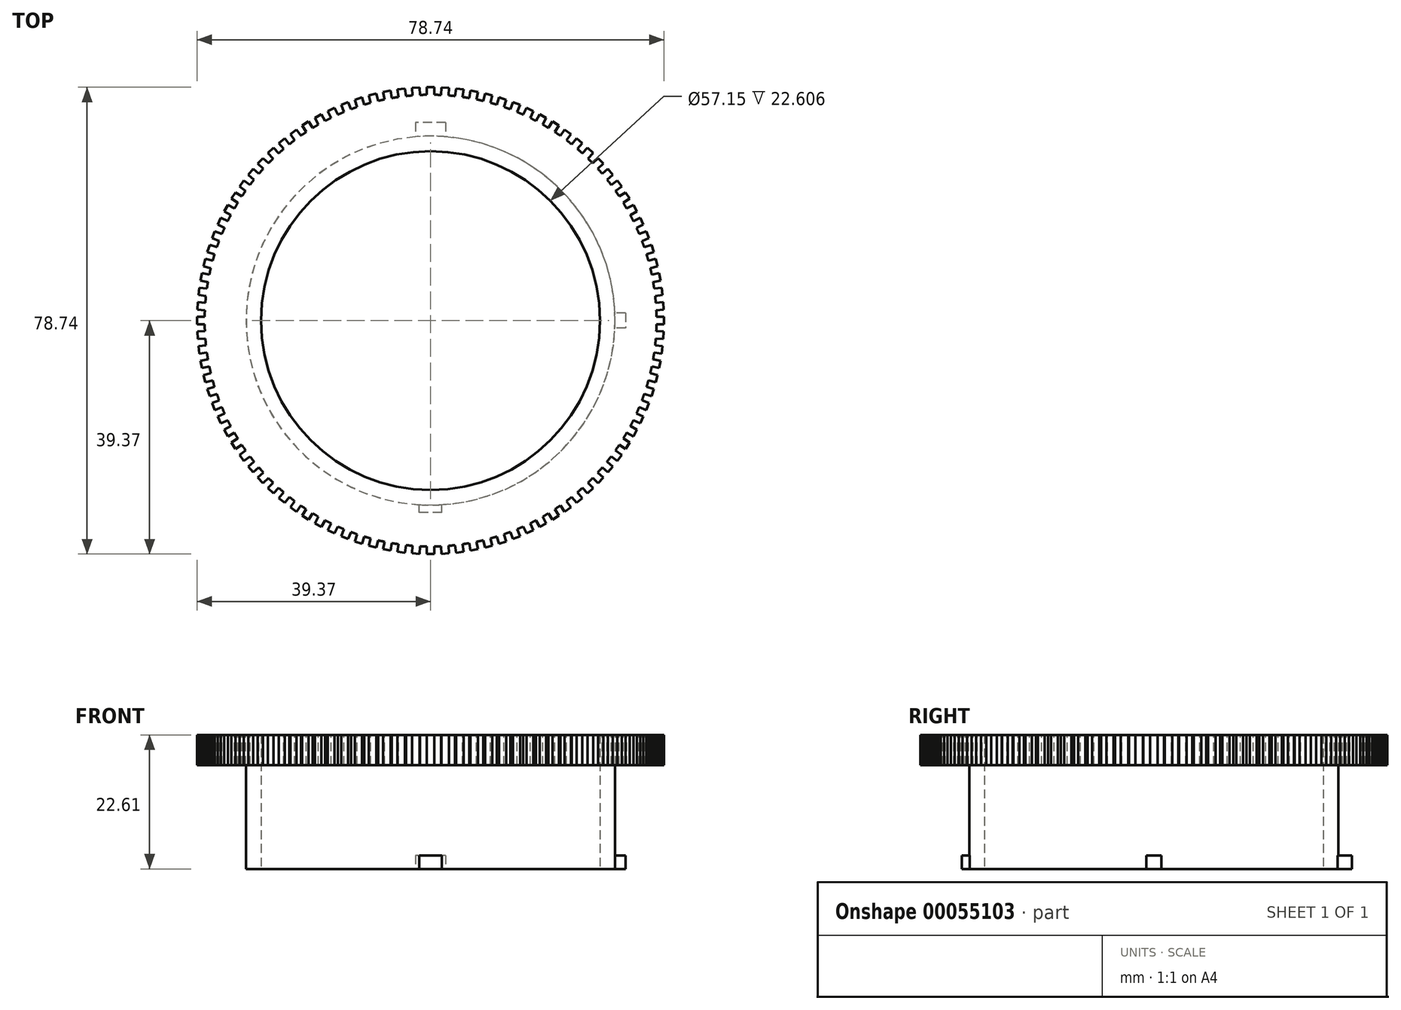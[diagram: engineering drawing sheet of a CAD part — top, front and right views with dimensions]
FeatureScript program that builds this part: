
annotation { "Feature Type Name" : "Feature", "Feature Type Description" : "" }
export const myFeature = defineFeature(function(context is Context, id is Id, definition is map)
    precondition{}
    {
        {
            var Q0;
            Q0=qCreatedBy(makeId("Top.planeOp"),FACE);
            var sketch = newSketch(context, id + "F0", { "sketchPlane" : qUnion([Q0])});
            skArc(sketch, "E0", {"start": v(-2.54, 31.01) * mm, "mid": v(-31.11, -0.32) * mm, "end": v(-1.9, -31.06) * mm});
            skLineSegment(sketch, "E1.rect.bottom", {"start": v(2.54, 33.4) * mm, "end": v(-2.54, 33.4) * mm});
            skLineSegment(sketch, "E1.rect.left", {"start": v(2.54, 33.4) * mm, "end": v(2.54, 31.01) * mm});
            skLineSegment(sketch, "E1.rect.right", {"start": v(-2.54, 33.4) * mm, "end": v(-2.54, 31.01) * mm});
            skPoint(sketch, "E1.rect.middle", {"position": v(0, 31.12) * mm});
            skLineSegment(sketch, "E2.rect.bottom", {"start": v(32.9, 1.27) * mm, "end": v(31.09, 1.27) * mm});
            skLineSegment(sketch, "E2.rect.top", {"start": v(32.9, -1.27) * mm, "end": v(31.09, -1.27) * mm});
            skLineSegment(sketch, "E2.rect.left", {"start": v(32.9, 1.27) * mm, "end": v(32.9, -1.27) * mm});
            skPoint(sketch, "E2.rect.middle", {"position": v(31.12, 0) * mm});
            skLineSegment(sketch, "E3.rect.bottom", {"start": v(1.9, -32.39) * mm, "end": v(-1.9, -32.39) * mm});
            skLineSegment(sketch, "E3.rect.left", {"start": v(1.9, -32.38) * mm, "end": v(1.9, -31.06) * mm});
            skLineSegment(sketch, "E3.rect.right", {"start": v(-1.9, -32.39) * mm, "end": v(-1.9, -31.06) * mm});
            skPoint(sketch, "E3.rect.middle", {"position": v(0, -31.12) * mm});
            skCircle(sketch, "E4", {"center": v(0, 0) * mm, "radius": 28.58 * mm});
            skPoint(sketch, "E1.rect.top.end.orphan", {"position": v(-2.54, 28.83) * mm});
            skPoint(sketch, "E5.orphan", {"position": v(2.54, 28.83) * mm});
            skArc(sketch, "E6.trimOffspring", {"start": v(31.09, 1.27) * mm, "mid": v(22.45, 21.55) * mm, "end": v(2.54, 31.01) * mm});
            skPoint(sketch, "E2.rect.right.end.orphan", {"position": v(29.34, -1.27) * mm});
            skPoint(sketch, "E2.rect.right.start.orphan", {"position": v(29.34, 1.27) * mm});
            skPoint(sketch, "E7.orphan", {"position": v(-1.9, -29.85) * mm});
            skArc(sketch, "E8.trimOffspring", {"start": v(1.9, -31.06) * mm, "mid": v(22.23, -21.78) * mm, "end": v(31.09, -1.27) * mm});
            skPoint(sketch, "E9.orphan", {"position": v(1.9, -29.85) * mm});
            skSolve(sketch);
        }
        {
            var Q0;
            Q0 = qSketchRegion(id + "F0", true);
            extrude(context, id + "F1", {"entities" : qUnion([Q0]), "depth" : 2.3 * mm});
        }
        {
            var Q0;
            Q0=makeQuery(id+"F1.opExtrude","CAP_FACE",FACE,{"disambiguationData":[OSD([sQuery(id+"F0.wireOp",EDGE,"E0"),sQuery(id+"F0.wireOp",EDGE,"E1.rect.bottom"),sQuery(id+"F0.wireOp",EDGE,"E1.rect.left"),sQuery(id+"F0.wireOp",EDGE,"E1.rect.right"),sQuery(id+"F0.wireOp",EDGE,"E2.rect.bottom"),sQuery(id+"F0.wireOp",EDGE,"E2.rect.top"),sQuery(id+"F0.wireOp",EDGE,"E2.rect.left"),sQuery(id+"F0.wireOp",EDGE,"E3.rect.bottom"),sQuery(id+"F0.wireOp",EDGE,"E3.rect.left"),sQuery(id+"F0.wireOp",EDGE,"E3.rect.right"),sQuery(id+"F0.wireOp",EDGE,"E4"),sQuery(id+"F0.wireOp",EDGE,"E6.trimOffspring"),sQuery(id+"F0.wireOp",EDGE,"E8.trimOffspring")])],"isStart":false});
            var sketch = newSketch(context, id + "F2", { "sketchPlane" : qUnion([Q0])});
            skCircle(sketch, "E10", {"center": v(0, 0) * mm, "radius": 28.58 * mm});
            skCircle(sketch, "E11", {"center": v(0, 0) * mm, "radius": 31.12 * mm});
            skSolve(sketch);
        }
        {
            var Q0;
            Q0 = qSketchRegion(id + "F2", true);
            extrude(context, id + "F3", {"entities" : qUnion([Q0]), "operationType" : NewBodyOperationType.ADD, "depth" : 16.5 * mm});
        }
        {
            var Q0;
            Q0=makeQuery(id+"F3.opExtrude","CAP_FACE",FACE,{"disambiguationData":[OSD([sQuery(id+"F2.wireOp",EDGE,"E10"),sQuery(id+"F2.wireOp",EDGE,"E11")])],"isStart":false});
            var sketch = newSketch(context, id + "F4", { "sketchPlane" : qUnion([Q0])});
            skCircle(sketch, "E12", {"center": v(0, 0) * mm, "radius": 28.57 * mm});
            skCircle(sketch, "E13", {"center": v(0, 0) * mm, "radius": 38.1 * mm});
            skSolve(sketch);
        }
        {
            var Q0;
            Q0 = qSketchRegion(id + "F4", true);
            extrude(context, id + "F5", {"entities" : qUnion([Q0]), "operationType" : NewBodyOperationType.ADD, "depth" : 3.8 * mm});
        }
        {
            var Q0;
            Q0=makeQuery(id+"F5.opExtrude","CAP_FACE",FACE,{"disambiguationData":[OSD([sQuery(id+"F4.wireOp",EDGE,"E12"),sQuery(id+"F4.wireOp",EDGE,"E13")])],"isStart":false});
            var sketch = newSketch(context, id + "F6", { "sketchPlane" : qUnion([Q0])});
            skCircle(sketch, "E14.0.0", {"center": v(0, 0) * mm, "radius": 38.1 * mm});
            skLineSegment(sketch, "E15.rect.bottom", {"start": v(0.64, -39.37) * mm, "end": v(-0.63, -39.37) * mm});
            skLineSegment(sketch, "E15.rect.left", {"start": v(0.64, -39.37) * mm, "end": v(0.64, -38.1) * mm});
            skLineSegment(sketch, "E15.rect.right", {"start": v(-0.63, -39.37) * mm, "end": v(-0.63, -38.1) * mm});
            skPoint(sketch, "E15.rect.middle", {"position": v(0, -38.1) * mm});
            skPoint(sketch, "E15.rect.top.end.orphan", {"position": v(-0.63, -36.83) * mm});
            skPoint(sketch, "E16.orphan", {"position": v(0.64, -36.83) * mm});
            skLineSegment(sketch, "E17.1.0", {"start": v(1.84, -39.33) * mm, "end": v(1.76, -38.06) * mm});
            skLineSegment(sketch, "E17.1.1", {"start": v(3.1, -39.25) * mm, "end": v(1.84, -39.33) * mm});
            skLineSegment(sketch, "E17.1.2", {"start": v(3.1, -39.25) * mm, "end": v(3.03, -37.98) * mm});
            skLineSegment(sketch, "E17.2.0", {"start": v(4.3, -39.14) * mm, "end": v(4.14, -37.87) * mm});
            skLineSegment(sketch, "E17.2.1", {"start": v(5.56, -38.98) * mm, "end": v(4.3, -39.14) * mm});
            skLineSegment(sketch, "E17.2.2", {"start": v(5.56, -38.98) * mm, "end": v(5.4, -37.71) * mm});
            skLineSegment(sketch, "E17.3.0", {"start": v(6.75, -38.8) * mm, "end": v(6.51, -37.54) * mm});
            skLineSegment(sketch, "E17.3.1", {"start": v(8, -38.55) * mm, "end": v(6.75, -38.8) * mm});
            skLineSegment(sketch, "E17.3.2", {"start": v(8, -38.55) * mm, "end": v(7.76, -37.3) * mm});
            skLineSegment(sketch, "E17.4.0", {"start": v(9.18, -38.3) * mm, "end": v(8.86, -37.06) * mm});
            skLineSegment(sketch, "E17.4.1", {"start": v(10.4, -37.98) * mm, "end": v(9.18, -38.3) * mm});
            skLineSegment(sketch, "E17.4.2", {"start": v(10.4, -37.98) * mm, "end": v(10.09, -36.74) * mm});
            skLineSegment(sketch, "E17.5.0", {"start": v(11.56, -37.64) * mm, "end": v(11.17, -36.43) * mm});
            skLineSegment(sketch, "E17.5.1", {"start": v(12.77, -37.25) * mm, "end": v(11.56, -37.64) * mm});
            skLineSegment(sketch, "E17.5.2", {"start": v(12.77, -37.25) * mm, "end": v(12.38, -36.03) * mm});
            skLineSegment(sketch, "E17.6.0", {"start": v(13.9, -36.84) * mm, "end": v(13.43, -35.65) * mm});
            skLineSegment(sketch, "E17.6.1", {"start": v(15.08, -36.37) * mm, "end": v(13.9, -36.84) * mm});
            skLineSegment(sketch, "E17.6.2", {"start": v(15.08, -36.37) * mm, "end": v(14.61, -35.19) * mm});
            skLineSegment(sketch, "E17.7.0", {"start": v(16.19, -35.9) * mm, "end": v(15.65, -34.74) * mm});
            skLineSegment(sketch, "E17.7.1", {"start": v(17.34, -35.35) * mm, "end": v(16.19, -35.9) * mm});
            skLineSegment(sketch, "E17.7.2", {"start": v(17.34, -35.35) * mm, "end": v(16.8, -34.2) * mm});
            skLineSegment(sketch, "E17.8.0", {"start": v(18.41, -34.8) * mm, "end": v(17.8, -33.69) * mm});
            skLineSegment(sketch, "E17.8.1", {"start": v(19.52, -34.2) * mm, "end": v(18.41, -34.8) * mm});
            skLineSegment(sketch, "E17.8.2", {"start": v(19.52, -34.2) * mm, "end": v(18.9, -33.08) * mm});
            skLineSegment(sketch, "E17.9.0", {"start": v(20.56, -33.58) * mm, "end": v(19.88, -32.5) * mm});
            skLineSegment(sketch, "E17.9.1", {"start": v(21.63, -32.9) * mm, "end": v(20.56, -33.58) * mm});
            skLineSegment(sketch, "E17.9.2", {"start": v(21.63, -32.9) * mm, "end": v(20.95, -31.82) * mm});
            skLineSegment(sketch, "E17.10.0", {"start": v(22.63, -32.22) * mm, "end": v(21.88, -31.2) * mm});
            skLineSegment(sketch, "E17.10.1", {"start": v(23.65, -31.48) * mm, "end": v(22.63, -32.22) * mm});
            skLineSegment(sketch, "E17.10.2", {"start": v(23.65, -31.48) * mm, "end": v(22.9, -30.45) * mm});
            skLineSegment(sketch, "E17.11.0", {"start": v(24.6, -30.74) * mm, "end": v(23.8, -29.76) * mm});
            skLineSegment(sketch, "E17.11.1", {"start": v(25.58, -29.93) * mm, "end": v(24.6, -30.74) * mm});
            skLineSegment(sketch, "E17.11.2", {"start": v(25.58, -29.93) * mm, "end": v(24.77, -28.95) * mm});
            skLineSegment(sketch, "E17.12.0", {"start": v(26.49, -29.13) * mm, "end": v(25.61, -28.2) * mm});
            skLineSegment(sketch, "E17.12.1", {"start": v(27.41, -28.26) * mm, "end": v(26.49, -29.13) * mm});
            skLineSegment(sketch, "E17.12.2", {"start": v(27.41, -28.26) * mm, "end": v(26.54, -27.34) * mm});
            skLineSegment(sketch, "E17.13.0", {"start": v(28.26, -27.41) * mm, "end": v(27.34, -26.54) * mm});
            skLineSegment(sketch, "E17.13.1", {"start": v(29.13, -26.49) * mm, "end": v(28.26, -27.41) * mm});
            skLineSegment(sketch, "E17.13.2", {"start": v(29.13, -26.49) * mm, "end": v(28.2, -25.61) * mm});
            skLineSegment(sketch, "E17.14.0", {"start": v(29.93, -25.58) * mm, "end": v(28.95, -24.77) * mm});
            skLineSegment(sketch, "E17.14.1", {"start": v(30.74, -24.6) * mm, "end": v(29.93, -25.58) * mm});
            skLineSegment(sketch, "E17.14.2", {"start": v(30.74, -24.6) * mm, "end": v(29.76, -23.8) * mm});
            skLineSegment(sketch, "E17.15.0", {"start": v(31.48, -23.65) * mm, "end": v(30.45, -22.9) * mm});
            skLineSegment(sketch, "E17.15.1", {"start": v(32.22, -22.63) * mm, "end": v(31.48, -23.65) * mm});
            skLineSegment(sketch, "E17.15.2", {"start": v(32.22, -22.63) * mm, "end": v(31.2, -21.88) * mm});
            skLineSegment(sketch, "E17.16.0", {"start": v(32.9, -21.63) * mm, "end": v(31.82, -20.95) * mm});
            skLineSegment(sketch, "E17.16.1", {"start": v(33.58, -20.56) * mm, "end": v(32.9, -21.63) * mm});
            skLineSegment(sketch, "E17.16.2", {"start": v(33.58, -20.56) * mm, "end": v(32.5, -19.88) * mm});
            skLineSegment(sketch, "E17.17.0", {"start": v(34.2, -19.52) * mm, "end": v(33.08, -18.9) * mm});
            skLineSegment(sketch, "E17.17.1", {"start": v(34.8, -18.41) * mm, "end": v(34.2, -19.52) * mm});
            skLineSegment(sketch, "E17.17.2", {"start": v(34.8, -18.41) * mm, "end": v(33.69, -17.8) * mm});
            skLineSegment(sketch, "E17.18.0", {"start": v(35.35, -17.34) * mm, "end": v(34.2, -16.8) * mm});
            skLineSegment(sketch, "E17.18.1", {"start": v(35.9, -16.19) * mm, "end": v(35.35, -17.34) * mm});
            skLineSegment(sketch, "E17.18.2", {"start": v(35.9, -16.19) * mm, "end": v(34.74, -15.65) * mm});
            skLineSegment(sketch, "E17.19.0", {"start": v(36.37, -15.08) * mm, "end": v(35.19, -14.61) * mm});
            skLineSegment(sketch, "E17.19.1", {"start": v(36.84, -13.9) * mm, "end": v(36.37, -15.08) * mm});
            skLineSegment(sketch, "E17.19.2", {"start": v(36.84, -13.9) * mm, "end": v(35.65, -13.43) * mm});
            skLineSegment(sketch, "E17.20.0", {"start": v(37.25, -12.77) * mm, "end": v(36.03, -12.38) * mm});
            skLineSegment(sketch, "E17.20.1", {"start": v(37.64, -11.56) * mm, "end": v(37.25, -12.77) * mm});
            skLineSegment(sketch, "E17.20.2", {"start": v(37.64, -11.56) * mm, "end": v(36.43, -11.17) * mm});
            skLineSegment(sketch, "E17.21.0", {"start": v(37.98, -10.4) * mm, "end": v(36.74, -10.09) * mm});
            skLineSegment(sketch, "E17.21.1", {"start": v(38.3, -9.18) * mm, "end": v(37.98, -10.4) * mm});
            skLineSegment(sketch, "E17.21.2", {"start": v(38.3, -9.18) * mm, "end": v(37.06, -8.86) * mm});
            skLineSegment(sketch, "E17.22.0", {"start": v(38.55, -8) * mm, "end": v(37.3, -7.76) * mm});
            skLineSegment(sketch, "E17.22.1", {"start": v(38.8, -6.75) * mm, "end": v(38.55, -8) * mm});
            skLineSegment(sketch, "E17.22.2", {"start": v(38.8, -6.75) * mm, "end": v(37.54, -6.51) * mm});
            skLineSegment(sketch, "E17.23.0", {"start": v(38.98, -5.56) * mm, "end": v(37.71, -5.4) * mm});
            skLineSegment(sketch, "E17.23.1", {"start": v(39.14, -4.3) * mm, "end": v(38.98, -5.56) * mm});
            skLineSegment(sketch, "E17.23.2", {"start": v(39.14, -4.3) * mm, "end": v(37.87, -4.14) * mm});
            skLineSegment(sketch, "E17.24.0", {"start": v(39.25, -3.1) * mm, "end": v(37.98, -3.03) * mm});
            skLineSegment(sketch, "E17.24.1", {"start": v(39.33, -1.84) * mm, "end": v(39.25, -3.1) * mm});
            skLineSegment(sketch, "E17.24.2", {"start": v(39.33, -1.84) * mm, "end": v(38.06, -1.76) * mm});
            skLineSegment(sketch, "E17.25.0", {"start": v(39.37, -0.63) * mm, "end": v(38.1, -0.63) * mm});
            skLineSegment(sketch, "E17.25.1", {"start": v(39.37, 0.64) * mm, "end": v(39.37, -0.63) * mm});
            skLineSegment(sketch, "E17.25.2", {"start": v(39.37, 0.64) * mm, "end": v(38.1, 0.64) * mm});
            skLineSegment(sketch, "E17.26.0", {"start": v(39.33, 1.84) * mm, "end": v(38.06, 1.76) * mm});
            skLineSegment(sketch, "E17.26.1", {"start": v(39.25, 3.1) * mm, "end": v(39.33, 1.84) * mm});
            skLineSegment(sketch, "E17.26.2", {"start": v(39.25, 3.1) * mm, "end": v(37.98, 3.03) * mm});
            skLineSegment(sketch, "E17.27.0", {"start": v(39.14, 4.3) * mm, "end": v(37.87, 4.14) * mm});
            skLineSegment(sketch, "E17.27.1", {"start": v(38.98, 5.56) * mm, "end": v(39.14, 4.3) * mm});
            skLineSegment(sketch, "E17.27.2", {"start": v(38.98, 5.56) * mm, "end": v(37.71, 5.4) * mm});
            skLineSegment(sketch, "E17.28.0", {"start": v(38.8, 6.75) * mm, "end": v(37.54, 6.51) * mm});
            skLineSegment(sketch, "E17.28.1", {"start": v(38.55, 8) * mm, "end": v(38.8, 6.75) * mm});
            skLineSegment(sketch, "E17.28.2", {"start": v(38.55, 8) * mm, "end": v(37.3, 7.76) * mm});
            skLineSegment(sketch, "E17.29.0", {"start": v(38.3, 9.18) * mm, "end": v(37.06, 8.86) * mm});
            skLineSegment(sketch, "E17.29.1", {"start": v(37.98, 10.4) * mm, "end": v(38.3, 9.18) * mm});
            skLineSegment(sketch, "E17.29.2", {"start": v(37.98, 10.4) * mm, "end": v(36.74, 10.09) * mm});
            skLineSegment(sketch, "E17.30.0", {"start": v(37.64, 11.56) * mm, "end": v(36.43, 11.17) * mm});
            skLineSegment(sketch, "E17.30.1", {"start": v(37.25, 12.77) * mm, "end": v(37.64, 11.56) * mm});
            skLineSegment(sketch, "E17.30.2", {"start": v(37.25, 12.77) * mm, "end": v(36.03, 12.38) * mm});
            skLineSegment(sketch, "E17.31.0", {"start": v(36.84, 13.9) * mm, "end": v(35.65, 13.43) * mm});
            skLineSegment(sketch, "E17.31.1", {"start": v(36.37, 15.08) * mm, "end": v(36.84, 13.9) * mm});
            skLineSegment(sketch, "E17.31.2", {"start": v(36.37, 15.08) * mm, "end": v(35.19, 14.61) * mm});
            skLineSegment(sketch, "E17.32.0", {"start": v(35.9, 16.19) * mm, "end": v(34.74, 15.65) * mm});
            skLineSegment(sketch, "E17.32.1", {"start": v(35.35, 17.34) * mm, "end": v(35.9, 16.19) * mm});
            skLineSegment(sketch, "E17.32.2", {"start": v(35.35, 17.34) * mm, "end": v(34.2, 16.8) * mm});
            skLineSegment(sketch, "E17.33.0", {"start": v(34.8, 18.41) * mm, "end": v(33.69, 17.8) * mm});
            skLineSegment(sketch, "E17.33.1", {"start": v(34.2, 19.52) * mm, "end": v(34.8, 18.41) * mm});
            skLineSegment(sketch, "E17.33.2", {"start": v(34.2, 19.52) * mm, "end": v(33.08, 18.9) * mm});
            skLineSegment(sketch, "E17.34.0", {"start": v(33.58, 20.56) * mm, "end": v(32.5, 19.88) * mm});
            skLineSegment(sketch, "E17.34.1", {"start": v(32.9, 21.63) * mm, "end": v(33.58, 20.56) * mm});
            skLineSegment(sketch, "E17.34.2", {"start": v(32.9, 21.63) * mm, "end": v(31.82, 20.95) * mm});
            skLineSegment(sketch, "E17.35.0", {"start": v(32.22, 22.63) * mm, "end": v(31.2, 21.88) * mm});
            skLineSegment(sketch, "E17.35.1", {"start": v(31.48, 23.65) * mm, "end": v(32.22, 22.63) * mm});
            skLineSegment(sketch, "E17.35.2", {"start": v(31.48, 23.65) * mm, "end": v(30.45, 22.9) * mm});
            skLineSegment(sketch, "E17.36.0", {"start": v(30.74, 24.6) * mm, "end": v(29.76, 23.8) * mm});
            skLineSegment(sketch, "E17.36.1", {"start": v(29.93, 25.58) * mm, "end": v(30.74, 24.6) * mm});
            skLineSegment(sketch, "E17.36.2", {"start": v(29.93, 25.58) * mm, "end": v(28.95, 24.77) * mm});
            skLineSegment(sketch, "E17.37.0", {"start": v(29.13, 26.49) * mm, "end": v(28.2, 25.61) * mm});
            skLineSegment(sketch, "E17.37.1", {"start": v(28.26, 27.41) * mm, "end": v(29.13, 26.49) * mm});
            skLineSegment(sketch, "E17.37.2", {"start": v(28.26, 27.41) * mm, "end": v(27.34, 26.54) * mm});
            skLineSegment(sketch, "E17.38.0", {"start": v(27.41, 28.26) * mm, "end": v(26.54, 27.34) * mm});
            skLineSegment(sketch, "E17.38.1", {"start": v(26.49, 29.13) * mm, "end": v(27.41, 28.26) * mm});
            skLineSegment(sketch, "E17.38.2", {"start": v(26.49, 29.13) * mm, "end": v(25.61, 28.2) * mm});
            skLineSegment(sketch, "E17.39.0", {"start": v(25.58, 29.93) * mm, "end": v(24.77, 28.95) * mm});
            skLineSegment(sketch, "E17.39.1", {"start": v(24.6, 30.74) * mm, "end": v(25.58, 29.93) * mm});
            skLineSegment(sketch, "E17.39.2", {"start": v(24.6, 30.74) * mm, "end": v(23.8, 29.76) * mm});
            skLineSegment(sketch, "E17.40.0", {"start": v(23.65, 31.48) * mm, "end": v(22.9, 30.45) * mm});
            skLineSegment(sketch, "E17.40.1", {"start": v(22.63, 32.22) * mm, "end": v(23.65, 31.48) * mm});
            skLineSegment(sketch, "E17.40.2", {"start": v(22.63, 32.22) * mm, "end": v(21.88, 31.2) * mm});
            skLineSegment(sketch, "E17.41.0", {"start": v(21.63, 32.9) * mm, "end": v(20.95, 31.82) * mm});
            skLineSegment(sketch, "E17.41.1", {"start": v(20.56, 33.58) * mm, "end": v(21.63, 32.9) * mm});
            skLineSegment(sketch, "E17.41.2", {"start": v(20.56, 33.58) * mm, "end": v(19.88, 32.5) * mm});
            skLineSegment(sketch, "E17.42.0", {"start": v(19.52, 34.2) * mm, "end": v(18.9, 33.08) * mm});
            skLineSegment(sketch, "E17.42.1", {"start": v(18.41, 34.8) * mm, "end": v(19.52, 34.2) * mm});
            skLineSegment(sketch, "E17.42.2", {"start": v(18.41, 34.8) * mm, "end": v(17.8, 33.69) * mm});
            skLineSegment(sketch, "E17.43.0", {"start": v(17.34, 35.35) * mm, "end": v(16.8, 34.2) * mm});
            skLineSegment(sketch, "E17.43.1", {"start": v(16.19, 35.9) * mm, "end": v(17.34, 35.35) * mm});
            skLineSegment(sketch, "E17.43.2", {"start": v(16.19, 35.9) * mm, "end": v(15.65, 34.74) * mm});
            skLineSegment(sketch, "E17.44.0", {"start": v(15.08, 36.37) * mm, "end": v(14.61, 35.19) * mm});
            skLineSegment(sketch, "E17.44.1", {"start": v(13.9, 36.84) * mm, "end": v(15.08, 36.37) * mm});
            skLineSegment(sketch, "E17.44.2", {"start": v(13.9, 36.84) * mm, "end": v(13.43, 35.65) * mm});
            skLineSegment(sketch, "E17.45.0", {"start": v(12.77, 37.25) * mm, "end": v(12.38, 36.03) * mm});
            skLineSegment(sketch, "E17.45.1", {"start": v(11.56, 37.64) * mm, "end": v(12.77, 37.25) * mm});
            skLineSegment(sketch, "E17.45.2", {"start": v(11.56, 37.64) * mm, "end": v(11.17, 36.43) * mm});
            skLineSegment(sketch, "E17.46.0", {"start": v(10.4, 37.98) * mm, "end": v(10.09, 36.74) * mm});
            skLineSegment(sketch, "E17.46.1", {"start": v(9.18, 38.3) * mm, "end": v(10.4, 37.98) * mm});
            skLineSegment(sketch, "E17.46.2", {"start": v(9.18, 38.3) * mm, "end": v(8.86, 37.06) * mm});
            skLineSegment(sketch, "E17.47.0", {"start": v(8, 38.55) * mm, "end": v(7.76, 37.3) * mm});
            skLineSegment(sketch, "E17.47.1", {"start": v(6.75, 38.8) * mm, "end": v(8, 38.55) * mm});
            skLineSegment(sketch, "E17.47.2", {"start": v(6.75, 38.8) * mm, "end": v(6.51, 37.54) * mm});
            skLineSegment(sketch, "E17.48.0", {"start": v(5.56, 38.98) * mm, "end": v(5.4, 37.71) * mm});
            skLineSegment(sketch, "E17.48.1", {"start": v(4.3, 39.14) * mm, "end": v(5.56, 38.98) * mm});
            skLineSegment(sketch, "E17.48.2", {"start": v(4.3, 39.14) * mm, "end": v(4.14, 37.87) * mm});
            skLineSegment(sketch, "E17.49.0", {"start": v(3.1, 39.25) * mm, "end": v(3.03, 37.98) * mm});
            skLineSegment(sketch, "E17.49.1", {"start": v(1.84, 39.33) * mm, "end": v(3.1, 39.25) * mm});
            skLineSegment(sketch, "E17.49.2", {"start": v(1.84, 39.33) * mm, "end": v(1.76, 38.06) * mm});
            skLineSegment(sketch, "E17.50.0", {"start": v(0.63, 39.37) * mm, "end": v(0.63, 38.1) * mm});
            skLineSegment(sketch, "E17.50.1", {"start": v(-0.64, 39.37) * mm, "end": v(0.63, 39.37) * mm});
            skLineSegment(sketch, "E17.50.2", {"start": v(-0.64, 39.37) * mm, "end": v(-0.64, 38.1) * mm});
            skLineSegment(sketch, "E17.51.0", {"start": v(-1.84, 39.33) * mm, "end": v(-1.76, 38.06) * mm});
            skLineSegment(sketch, "E17.51.1", {"start": v(-3.1, 39.25) * mm, "end": v(-1.84, 39.33) * mm});
            skLineSegment(sketch, "E17.51.2", {"start": v(-3.1, 39.25) * mm, "end": v(-3.03, 37.98) * mm});
            skLineSegment(sketch, "E17.52.0", {"start": v(-4.3, 39.14) * mm, "end": v(-4.14, 37.87) * mm});
            skLineSegment(sketch, "E17.52.1", {"start": v(-5.56, 38.98) * mm, "end": v(-4.3, 39.14) * mm});
            skLineSegment(sketch, "E17.52.2", {"start": v(-5.56, 38.98) * mm, "end": v(-5.4, 37.71) * mm});
            skLineSegment(sketch, "E17.53.0", {"start": v(-6.75, 38.8) * mm, "end": v(-6.51, 37.54) * mm});
            skLineSegment(sketch, "E17.53.1", {"start": v(-8, 38.55) * mm, "end": v(-6.75, 38.8) * mm});
            skLineSegment(sketch, "E17.53.2", {"start": v(-8, 38.55) * mm, "end": v(-7.76, 37.3) * mm});
            skLineSegment(sketch, "E17.54.0", {"start": v(-9.18, 38.3) * mm, "end": v(-8.86, 37.06) * mm});
            skLineSegment(sketch, "E17.54.1", {"start": v(-10.4, 37.98) * mm, "end": v(-9.18, 38.3) * mm});
            skLineSegment(sketch, "E17.54.2", {"start": v(-10.4, 37.98) * mm, "end": v(-10.09, 36.74) * mm});
            skLineSegment(sketch, "E17.55.0", {"start": v(-11.56, 37.64) * mm, "end": v(-11.17, 36.43) * mm});
            skLineSegment(sketch, "E17.55.1", {"start": v(-12.77, 37.25) * mm, "end": v(-11.56, 37.64) * mm});
            skLineSegment(sketch, "E17.55.2", {"start": v(-12.77, 37.25) * mm, "end": v(-12.38, 36.03) * mm});
            skLineSegment(sketch, "E17.56.0", {"start": v(-13.9, 36.84) * mm, "end": v(-13.43, 35.65) * mm});
            skLineSegment(sketch, "E17.56.1", {"start": v(-15.08, 36.37) * mm, "end": v(-13.9, 36.84) * mm});
            skLineSegment(sketch, "E17.56.2", {"start": v(-15.08, 36.37) * mm, "end": v(-14.61, 35.19) * mm});
            skLineSegment(sketch, "E17.57.0", {"start": v(-16.19, 35.9) * mm, "end": v(-15.65, 34.74) * mm});
            skLineSegment(sketch, "E17.57.1", {"start": v(-17.34, 35.35) * mm, "end": v(-16.19, 35.9) * mm});
            skLineSegment(sketch, "E17.57.2", {"start": v(-17.34, 35.35) * mm, "end": v(-16.8, 34.2) * mm});
            skLineSegment(sketch, "E17.58.0", {"start": v(-18.41, 34.8) * mm, "end": v(-17.8, 33.69) * mm});
            skLineSegment(sketch, "E17.58.1", {"start": v(-19.52, 34.2) * mm, "end": v(-18.41, 34.8) * mm});
            skLineSegment(sketch, "E17.58.2", {"start": v(-19.52, 34.2) * mm, "end": v(-18.9, 33.08) * mm});
            skLineSegment(sketch, "E17.59.0", {"start": v(-20.56, 33.58) * mm, "end": v(-19.88, 32.5) * mm});
            skLineSegment(sketch, "E17.59.1", {"start": v(-21.63, 32.9) * mm, "end": v(-20.56, 33.58) * mm});
            skLineSegment(sketch, "E17.59.2", {"start": v(-21.63, 32.9) * mm, "end": v(-20.95, 31.82) * mm});
            skLineSegment(sketch, "E17.60.0", {"start": v(-22.63, 32.22) * mm, "end": v(-21.88, 31.2) * mm});
            skLineSegment(sketch, "E17.60.1", {"start": v(-23.65, 31.48) * mm, "end": v(-22.63, 32.22) * mm});
            skLineSegment(sketch, "E17.60.2", {"start": v(-23.65, 31.48) * mm, "end": v(-22.9, 30.45) * mm});
            skLineSegment(sketch, "E17.61.0", {"start": v(-24.6, 30.74) * mm, "end": v(-23.8, 29.76) * mm});
            skLineSegment(sketch, "E17.61.1", {"start": v(-25.58, 29.93) * mm, "end": v(-24.6, 30.74) * mm});
            skLineSegment(sketch, "E17.61.2", {"start": v(-25.58, 29.93) * mm, "end": v(-24.77, 28.95) * mm});
            skLineSegment(sketch, "E17.62.0", {"start": v(-26.49, 29.13) * mm, "end": v(-25.61, 28.2) * mm});
            skLineSegment(sketch, "E17.62.1", {"start": v(-27.41, 28.26) * mm, "end": v(-26.49, 29.13) * mm});
            skLineSegment(sketch, "E17.62.2", {"start": v(-27.41, 28.26) * mm, "end": v(-26.54, 27.34) * mm});
            skLineSegment(sketch, "E17.63.0", {"start": v(-28.26, 27.41) * mm, "end": v(-27.34, 26.54) * mm});
            skLineSegment(sketch, "E17.63.1", {"start": v(-29.13, 26.49) * mm, "end": v(-28.26, 27.41) * mm});
            skLineSegment(sketch, "E17.63.2", {"start": v(-29.13, 26.49) * mm, "end": v(-28.2, 25.61) * mm});
            skLineSegment(sketch, "E17.64.0", {"start": v(-29.93, 25.58) * mm, "end": v(-28.95, 24.77) * mm});
            skLineSegment(sketch, "E17.64.1", {"start": v(-30.74, 24.6) * mm, "end": v(-29.93, 25.58) * mm});
            skLineSegment(sketch, "E17.64.2", {"start": v(-30.74, 24.6) * mm, "end": v(-29.76, 23.8) * mm});
            skLineSegment(sketch, "E17.65.0", {"start": v(-31.48, 23.65) * mm, "end": v(-30.45, 22.9) * mm});
            skLineSegment(sketch, "E17.65.1", {"start": v(-32.22, 22.63) * mm, "end": v(-31.48, 23.65) * mm});
            skLineSegment(sketch, "E17.65.2", {"start": v(-32.22, 22.63) * mm, "end": v(-31.2, 21.88) * mm});
            skLineSegment(sketch, "E17.66.0", {"start": v(-32.9, 21.63) * mm, "end": v(-31.82, 20.95) * mm});
            skLineSegment(sketch, "E17.66.1", {"start": v(-33.58, 20.56) * mm, "end": v(-32.9, 21.63) * mm});
            skLineSegment(sketch, "E17.66.2", {"start": v(-33.58, 20.56) * mm, "end": v(-32.5, 19.88) * mm});
            skLineSegment(sketch, "E17.67.0", {"start": v(-34.2, 19.52) * mm, "end": v(-33.08, 18.9) * mm});
            skLineSegment(sketch, "E17.67.1", {"start": v(-34.8, 18.41) * mm, "end": v(-34.2, 19.52) * mm});
            skLineSegment(sketch, "E17.67.2", {"start": v(-34.8, 18.41) * mm, "end": v(-33.69, 17.8) * mm});
            skLineSegment(sketch, "E17.68.0", {"start": v(-35.35, 17.34) * mm, "end": v(-34.2, 16.8) * mm});
            skLineSegment(sketch, "E17.68.1", {"start": v(-35.9, 16.19) * mm, "end": v(-35.35, 17.34) * mm});
            skLineSegment(sketch, "E17.68.2", {"start": v(-35.9, 16.19) * mm, "end": v(-34.74, 15.65) * mm});
            skLineSegment(sketch, "E17.69.0", {"start": v(-36.37, 15.08) * mm, "end": v(-35.19, 14.61) * mm});
            skLineSegment(sketch, "E17.69.1", {"start": v(-36.84, 13.9) * mm, "end": v(-36.37, 15.08) * mm});
            skLineSegment(sketch, "E17.69.2", {"start": v(-36.84, 13.9) * mm, "end": v(-35.65, 13.43) * mm});
            skLineSegment(sketch, "E17.70.0", {"start": v(-37.25, 12.77) * mm, "end": v(-36.03, 12.38) * mm});
            skLineSegment(sketch, "E17.70.1", {"start": v(-37.64, 11.56) * mm, "end": v(-37.25, 12.77) * mm});
            skLineSegment(sketch, "E17.70.2", {"start": v(-37.64, 11.56) * mm, "end": v(-36.43, 11.17) * mm});
            skLineSegment(sketch, "E17.71.0", {"start": v(-37.98, 10.4) * mm, "end": v(-36.74, 10.09) * mm});
            skLineSegment(sketch, "E17.71.1", {"start": v(-38.3, 9.18) * mm, "end": v(-37.98, 10.4) * mm});
            skLineSegment(sketch, "E17.71.2", {"start": v(-38.3, 9.18) * mm, "end": v(-37.06, 8.86) * mm});
            skLineSegment(sketch, "E17.72.0", {"start": v(-38.55, 8) * mm, "end": v(-37.3, 7.76) * mm});
            skLineSegment(sketch, "E17.72.1", {"start": v(-38.8, 6.75) * mm, "end": v(-38.55, 8) * mm});
            skLineSegment(sketch, "E17.72.2", {"start": v(-38.8, 6.75) * mm, "end": v(-37.54, 6.51) * mm});
            skLineSegment(sketch, "E17.73.0", {"start": v(-38.98, 5.56) * mm, "end": v(-37.71, 5.4) * mm});
            skLineSegment(sketch, "E17.73.1", {"start": v(-39.14, 4.3) * mm, "end": v(-38.98, 5.56) * mm});
            skLineSegment(sketch, "E17.73.2", {"start": v(-39.14, 4.3) * mm, "end": v(-37.87, 4.14) * mm});
            skLineSegment(sketch, "E17.74.0", {"start": v(-39.25, 3.1) * mm, "end": v(-37.98, 3.03) * mm});
            skLineSegment(sketch, "E17.74.1", {"start": v(-39.33, 1.84) * mm, "end": v(-39.25, 3.1) * mm});
            skLineSegment(sketch, "E17.74.2", {"start": v(-39.33, 1.84) * mm, "end": v(-38.06, 1.76) * mm});
            skLineSegment(sketch, "E17.75.0", {"start": v(-39.37, 0.64) * mm, "end": v(-38.1, 0.63) * mm});
            skLineSegment(sketch, "E17.75.1", {"start": v(-39.37, -0.63) * mm, "end": v(-39.37, 0.64) * mm});
            skLineSegment(sketch, "E17.75.2", {"start": v(-39.37, -0.64) * mm, "end": v(-38.1, -0.64) * mm});
            skLineSegment(sketch, "E17.76.0", {"start": v(-39.33, -1.84) * mm, "end": v(-38.06, -1.76) * mm});
            skLineSegment(sketch, "E17.76.1", {"start": v(-39.25, -3.1) * mm, "end": v(-39.33, -1.84) * mm});
            skLineSegment(sketch, "E17.76.2", {"start": v(-39.25, -3.1) * mm, "end": v(-37.98, -3.03) * mm});
            skLineSegment(sketch, "E17.77.0", {"start": v(-39.14, -4.3) * mm, "end": v(-37.87, -4.14) * mm});
            skLineSegment(sketch, "E17.77.1", {"start": v(-38.98, -5.56) * mm, "end": v(-39.14, -4.3) * mm});
            skLineSegment(sketch, "E17.77.2", {"start": v(-38.98, -5.56) * mm, "end": v(-37.71, -5.4) * mm});
            skLineSegment(sketch, "E17.78.0", {"start": v(-38.8, -6.75) * mm, "end": v(-37.54, -6.51) * mm});
            skLineSegment(sketch, "E17.78.1", {"start": v(-38.55, -8) * mm, "end": v(-38.8, -6.75) * mm});
            skLineSegment(sketch, "E17.78.2", {"start": v(-38.55, -8) * mm, "end": v(-37.3, -7.76) * mm});
            skLineSegment(sketch, "E17.79.0", {"start": v(-38.3, -9.18) * mm, "end": v(-37.06, -8.86) * mm});
            skLineSegment(sketch, "E17.79.1", {"start": v(-37.98, -10.4) * mm, "end": v(-38.3, -9.18) * mm});
            skLineSegment(sketch, "E17.79.2", {"start": v(-37.98, -10.4) * mm, "end": v(-36.74, -10.09) * mm});
            skLineSegment(sketch, "E17.80.0", {"start": v(-37.64, -11.56) * mm, "end": v(-36.43, -11.17) * mm});
            skLineSegment(sketch, "E17.80.1", {"start": v(-37.25, -12.77) * mm, "end": v(-37.64, -11.56) * mm});
            skLineSegment(sketch, "E17.80.2", {"start": v(-37.25, -12.77) * mm, "end": v(-36.03, -12.38) * mm});
            skLineSegment(sketch, "E17.81.0", {"start": v(-36.84, -13.9) * mm, "end": v(-35.65, -13.43) * mm});
            skLineSegment(sketch, "E17.81.1", {"start": v(-36.37, -15.08) * mm, "end": v(-36.84, -13.9) * mm});
            skLineSegment(sketch, "E17.81.2", {"start": v(-36.37, -15.08) * mm, "end": v(-35.19, -14.61) * mm});
            skLineSegment(sketch, "E17.82.0", {"start": v(-35.9, -16.19) * mm, "end": v(-34.74, -15.65) * mm});
            skLineSegment(sketch, "E17.82.1", {"start": v(-35.35, -17.34) * mm, "end": v(-35.9, -16.19) * mm});
            skLineSegment(sketch, "E17.82.2", {"start": v(-35.35, -17.34) * mm, "end": v(-34.2, -16.8) * mm});
            skLineSegment(sketch, "E17.83.0", {"start": v(-34.8, -18.41) * mm, "end": v(-33.69, -17.8) * mm});
            skLineSegment(sketch, "E17.83.1", {"start": v(-34.2, -19.52) * mm, "end": v(-34.8, -18.41) * mm});
            skLineSegment(sketch, "E17.83.2", {"start": v(-34.2, -19.52) * mm, "end": v(-33.08, -18.9) * mm});
            skLineSegment(sketch, "E17.84.0", {"start": v(-33.58, -20.56) * mm, "end": v(-32.5, -19.88) * mm});
            skLineSegment(sketch, "E17.84.1", {"start": v(-32.9, -21.63) * mm, "end": v(-33.58, -20.56) * mm});
            skLineSegment(sketch, "E17.84.2", {"start": v(-32.9, -21.63) * mm, "end": v(-31.82, -20.95) * mm});
            skLineSegment(sketch, "E17.85.0", {"start": v(-32.22, -22.63) * mm, "end": v(-31.2, -21.88) * mm});
            skLineSegment(sketch, "E17.85.1", {"start": v(-31.48, -23.65) * mm, "end": v(-32.22, -22.63) * mm});
            skLineSegment(sketch, "E17.85.2", {"start": v(-31.48, -23.65) * mm, "end": v(-30.45, -22.9) * mm});
            skLineSegment(sketch, "E17.86.0", {"start": v(-30.74, -24.6) * mm, "end": v(-29.76, -23.8) * mm});
            skLineSegment(sketch, "E17.86.1", {"start": v(-29.93, -25.58) * mm, "end": v(-30.74, -24.6) * mm});
            skLineSegment(sketch, "E17.86.2", {"start": v(-29.93, -25.58) * mm, "end": v(-28.95, -24.77) * mm});
            skLineSegment(sketch, "E17.87.0", {"start": v(-29.13, -26.49) * mm, "end": v(-28.2, -25.61) * mm});
            skLineSegment(sketch, "E17.87.1", {"start": v(-28.26, -27.41) * mm, "end": v(-29.13, -26.49) * mm});
            skLineSegment(sketch, "E17.87.2", {"start": v(-28.26, -27.41) * mm, "end": v(-27.34, -26.54) * mm});
            skLineSegment(sketch, "E17.88.0", {"start": v(-27.41, -28.26) * mm, "end": v(-26.54, -27.34) * mm});
            skLineSegment(sketch, "E17.88.1", {"start": v(-26.49, -29.13) * mm, "end": v(-27.41, -28.26) * mm});
            skLineSegment(sketch, "E17.88.2", {"start": v(-26.49, -29.13) * mm, "end": v(-25.61, -28.2) * mm});
            skLineSegment(sketch, "E17.89.0", {"start": v(-25.58, -29.93) * mm, "end": v(-24.77, -28.95) * mm});
            skLineSegment(sketch, "E17.89.1", {"start": v(-24.6, -30.74) * mm, "end": v(-25.58, -29.93) * mm});
            skLineSegment(sketch, "E17.89.2", {"start": v(-24.6, -30.74) * mm, "end": v(-23.8, -29.76) * mm});
            skLineSegment(sketch, "E17.90.0", {"start": v(-23.65, -31.48) * mm, "end": v(-22.9, -30.45) * mm});
            skLineSegment(sketch, "E17.90.1", {"start": v(-22.63, -32.22) * mm, "end": v(-23.65, -31.48) * mm});
            skLineSegment(sketch, "E17.90.2", {"start": v(-22.63, -32.22) * mm, "end": v(-21.88, -31.2) * mm});
            skLineSegment(sketch, "E17.91.0", {"start": v(-21.63, -32.9) * mm, "end": v(-20.95, -31.82) * mm});
            skLineSegment(sketch, "E17.91.1", {"start": v(-20.56, -33.58) * mm, "end": v(-21.63, -32.9) * mm});
            skLineSegment(sketch, "E17.91.2", {"start": v(-20.56, -33.58) * mm, "end": v(-19.88, -32.5) * mm});
            skLineSegment(sketch, "E17.92.0", {"start": v(-19.52, -34.2) * mm, "end": v(-18.9, -33.08) * mm});
            skLineSegment(sketch, "E17.92.1", {"start": v(-18.41, -34.8) * mm, "end": v(-19.52, -34.2) * mm});
            skLineSegment(sketch, "E17.92.2", {"start": v(-18.41, -34.8) * mm, "end": v(-17.8, -33.69) * mm});
            skLineSegment(sketch, "E17.93.0", {"start": v(-17.34, -35.35) * mm, "end": v(-16.8, -34.2) * mm});
            skLineSegment(sketch, "E17.93.1", {"start": v(-16.19, -35.9) * mm, "end": v(-17.34, -35.35) * mm});
            skLineSegment(sketch, "E17.93.2", {"start": v(-16.19, -35.9) * mm, "end": v(-15.65, -34.74) * mm});
            skLineSegment(sketch, "E17.94.0", {"start": v(-15.08, -36.37) * mm, "end": v(-14.61, -35.19) * mm});
            skLineSegment(sketch, "E17.94.1", {"start": v(-13.9, -36.84) * mm, "end": v(-15.08, -36.37) * mm});
            skLineSegment(sketch, "E17.94.2", {"start": v(-13.9, -36.84) * mm, "end": v(-13.43, -35.65) * mm});
            skLineSegment(sketch, "E17.95.0", {"start": v(-12.77, -37.25) * mm, "end": v(-12.38, -36.03) * mm});
            skLineSegment(sketch, "E17.95.1", {"start": v(-11.56, -37.64) * mm, "end": v(-12.77, -37.25) * mm});
            skLineSegment(sketch, "E17.95.2", {"start": v(-11.56, -37.64) * mm, "end": v(-11.17, -36.43) * mm});
            skLineSegment(sketch, "E17.96.0", {"start": v(-10.4, -37.98) * mm, "end": v(-10.09, -36.74) * mm});
            skLineSegment(sketch, "E17.96.1", {"start": v(-9.18, -38.3) * mm, "end": v(-10.4, -37.98) * mm});
            skLineSegment(sketch, "E17.96.2", {"start": v(-9.18, -38.3) * mm, "end": v(-8.86, -37.06) * mm});
            skLineSegment(sketch, "E17.97.0", {"start": v(-8, -38.55) * mm, "end": v(-7.76, -37.3) * mm});
            skLineSegment(sketch, "E17.97.1", {"start": v(-6.75, -38.8) * mm, "end": v(-8, -38.55) * mm});
            skLineSegment(sketch, "E17.97.2", {"start": v(-6.75, -38.8) * mm, "end": v(-6.51, -37.54) * mm});
            skLineSegment(sketch, "E17.98.0", {"start": v(-5.56, -38.98) * mm, "end": v(-5.4, -37.71) * mm});
            skLineSegment(sketch, "E17.98.1", {"start": v(-4.3, -39.14) * mm, "end": v(-5.56, -38.98) * mm});
            skLineSegment(sketch, "E17.98.2", {"start": v(-4.3, -39.14) * mm, "end": v(-4.14, -37.87) * mm});
            skLineSegment(sketch, "E17.99.0", {"start": v(-3.1, -39.25) * mm, "end": v(-3.03, -37.98) * mm});
            skLineSegment(sketch, "E17.99.1", {"start": v(-1.84, -39.33) * mm, "end": v(-3.1, -39.25) * mm});
            skLineSegment(sketch, "E17.99.2", {"start": v(-1.84, -39.33) * mm, "end": v(-1.76, -38.06) * mm});
            skSolve(sketch);
        }
        {
            var Q0;
            Q0=makeQuery(id+"F6.imprint","IMPRINT",FACE,{"disambiguationData":[TD([[makeQuery(id+"F6.imprint","IMPRINT",EDGE,{"derivedFrom":sQuery(id+"F6.wireOp",EDGE,"E15.rect.bottom")}),-1.0]])]});
            var Q1;
            {var subQ0=sQuery(id+"F6.wireOp",EDGE,"E17.1.0");Q1=makeQuery(id+"F6.imprint","IMPRINT",FACE,{"disambiguationData":[TD([[makeQuery(id+"F6.imprint","IMPRINT",EDGE,{"derivedFrom":subQ0}),-1.0]])]});}
            var Q2;
            {var subQ0=sQuery(id+"F6.wireOp",EDGE,"E17.2.0");Q2=makeQuery(id+"F6.imprint","IMPRINT",FACE,{"disambiguationData":[TD([[makeQuery(id+"F6.imprint","IMPRINT",EDGE,{"derivedFrom":subQ0}),-1.0]])]});}
            var Q3;
            {var subQ0=sQuery(id+"F6.wireOp",EDGE,"E17.3.0");Q3=makeQuery(id+"F6.imprint","IMPRINT",FACE,{"disambiguationData":[TD([[makeQuery(id+"F6.imprint","IMPRINT",EDGE,{"derivedFrom":subQ0}),-1.0]])]});}
            var Q4;
            {var subQ0=sQuery(id+"F6.wireOp",EDGE,"E17.4.0");Q4=makeQuery(id+"F6.imprint","IMPRINT",FACE,{"disambiguationData":[TD([[makeQuery(id+"F6.imprint","IMPRINT",EDGE,{"derivedFrom":subQ0}),-1.0]])]});}
            var Q5;
            {var subQ0=sQuery(id+"F6.wireOp",EDGE,"E17.5.0");Q5=makeQuery(id+"F6.imprint","IMPRINT",FACE,{"disambiguationData":[TD([[makeQuery(id+"F6.imprint","IMPRINT",EDGE,{"derivedFrom":subQ0}),-1.0]])]});}
            var Q6;
            {var subQ0=sQuery(id+"F6.wireOp",EDGE,"E17.6.0");Q6=makeQuery(id+"F6.imprint","IMPRINT",FACE,{"disambiguationData":[TD([[makeQuery(id+"F6.imprint","IMPRINT",EDGE,{"derivedFrom":subQ0}),-1.0]])]});}
            var Q7;
            {var subQ0=sQuery(id+"F6.wireOp",EDGE,"E17.7.0");Q7=makeQuery(id+"F6.imprint","IMPRINT",FACE,{"disambiguationData":[TD([[makeQuery(id+"F6.imprint","IMPRINT",EDGE,{"derivedFrom":subQ0}),-1.0]])]});}
            var Q8;
            {var subQ0=sQuery(id+"F6.wireOp",EDGE,"E17.8.0");Q8=makeQuery(id+"F6.imprint","IMPRINT",FACE,{"disambiguationData":[TD([[makeQuery(id+"F6.imprint","IMPRINT",EDGE,{"derivedFrom":subQ0}),-1.0]])]});}
            var Q9;
            {var subQ0=sQuery(id+"F6.wireOp",EDGE,"E17.9.0");Q9=makeQuery(id+"F6.imprint","IMPRINT",FACE,{"disambiguationData":[TD([[makeQuery(id+"F6.imprint","IMPRINT",EDGE,{"derivedFrom":subQ0}),-1.0]])]});}
            var Q10;
            {var subQ0=sQuery(id+"F6.wireOp",EDGE,"E17.10.0");Q10=makeQuery(id+"F6.imprint","IMPRINT",FACE,{"disambiguationData":[TD([[makeQuery(id+"F6.imprint","IMPRINT",EDGE,{"derivedFrom":subQ0}),-1.0]])]});}
            var Q11;
            {var subQ0=sQuery(id+"F6.wireOp",EDGE,"E17.11.0");Q11=makeQuery(id+"F6.imprint","IMPRINT",FACE,{"disambiguationData":[TD([[makeQuery(id+"F6.imprint","IMPRINT",EDGE,{"derivedFrom":subQ0}),-1.0]])]});}
            var Q12;
            {var subQ0=sQuery(id+"F6.wireOp",EDGE,"E17.12.0");Q12=makeQuery(id+"F6.imprint","IMPRINT",FACE,{"disambiguationData":[TD([[makeQuery(id+"F6.imprint","IMPRINT",EDGE,{"derivedFrom":subQ0}),-1.0]])]});}
            var Q13;
            {var subQ0=sQuery(id+"F6.wireOp",EDGE,"E17.13.0");Q13=makeQuery(id+"F6.imprint","IMPRINT",FACE,{"disambiguationData":[TD([[makeQuery(id+"F6.imprint","IMPRINT",EDGE,{"derivedFrom":subQ0}),-1.0]])]});}
            var Q14;
            {var subQ0=sQuery(id+"F6.wireOp",EDGE,"E17.14.0");Q14=makeQuery(id+"F6.imprint","IMPRINT",FACE,{"disambiguationData":[TD([[makeQuery(id+"F6.imprint","IMPRINT",EDGE,{"derivedFrom":subQ0}),-1.0]])]});}
            var Q15;
            {var subQ0=sQuery(id+"F6.wireOp",EDGE,"E17.15.0");Q15=makeQuery(id+"F6.imprint","IMPRINT",FACE,{"disambiguationData":[TD([[makeQuery(id+"F6.imprint","IMPRINT",EDGE,{"derivedFrom":subQ0}),-1.0]])]});}
            var Q16;
            {var subQ0=sQuery(id+"F6.wireOp",EDGE,"E17.16.0");Q16=makeQuery(id+"F6.imprint","IMPRINT",FACE,{"disambiguationData":[TD([[makeQuery(id+"F6.imprint","IMPRINT",EDGE,{"derivedFrom":subQ0}),-1.0]])]});}
            var Q17;
            {var subQ0=sQuery(id+"F6.wireOp",EDGE,"E17.17.0");Q17=makeQuery(id+"F6.imprint","IMPRINT",FACE,{"disambiguationData":[TD([[makeQuery(id+"F6.imprint","IMPRINT",EDGE,{"derivedFrom":subQ0}),-1.0]])]});}
            var Q18;
            {var subQ0=sQuery(id+"F6.wireOp",EDGE,"E17.18.0");Q18=makeQuery(id+"F6.imprint","IMPRINT",FACE,{"disambiguationData":[TD([[makeQuery(id+"F6.imprint","IMPRINT",EDGE,{"derivedFrom":subQ0}),-1.0]])]});}
            var Q19;
            {var subQ0=sQuery(id+"F6.wireOp",EDGE,"E17.19.0");Q19=makeQuery(id+"F6.imprint","IMPRINT",FACE,{"disambiguationData":[TD([[makeQuery(id+"F6.imprint","IMPRINT",EDGE,{"derivedFrom":subQ0}),-1.0]])]});}
            var Q20;
            {var subQ0=sQuery(id+"F6.wireOp",EDGE,"E17.20.0");Q20=makeQuery(id+"F6.imprint","IMPRINT",FACE,{"disambiguationData":[TD([[makeQuery(id+"F6.imprint","IMPRINT",EDGE,{"derivedFrom":subQ0}),-1.0]])]});}
            var Q21;
            {var subQ0=sQuery(id+"F6.wireOp",EDGE,"E17.21.0");Q21=makeQuery(id+"F6.imprint","IMPRINT",FACE,{"disambiguationData":[TD([[makeQuery(id+"F6.imprint","IMPRINT",EDGE,{"derivedFrom":subQ0}),-1.0]])]});}
            var Q22;
            {var subQ0=sQuery(id+"F6.wireOp",EDGE,"E17.22.0");Q22=makeQuery(id+"F6.imprint","IMPRINT",FACE,{"disambiguationData":[TD([[makeQuery(id+"F6.imprint","IMPRINT",EDGE,{"derivedFrom":subQ0}),-1.0]])]});}
            var Q23;
            {var subQ0=sQuery(id+"F6.wireOp",EDGE,"E17.23.0");Q23=makeQuery(id+"F6.imprint","IMPRINT",FACE,{"disambiguationData":[TD([[makeQuery(id+"F6.imprint","IMPRINT",EDGE,{"derivedFrom":subQ0}),-1.0]])]});}
            var Q24;
            {var subQ0=sQuery(id+"F6.wireOp",EDGE,"E17.24.0");Q24=makeQuery(id+"F6.imprint","IMPRINT",FACE,{"disambiguationData":[TD([[makeQuery(id+"F6.imprint","IMPRINT",EDGE,{"derivedFrom":subQ0}),-1.0]])]});}
            var Q25;
            {var subQ0=sQuery(id+"F6.wireOp",EDGE,"E17.25.0");Q25=makeQuery(id+"F6.imprint","IMPRINT",FACE,{"disambiguationData":[TD([[makeQuery(id+"F6.imprint","IMPRINT",EDGE,{"derivedFrom":subQ0}),-1.0]])]});}
            var Q26;
            {var subQ0=sQuery(id+"F6.wireOp",EDGE,"E17.26.0");Q26=makeQuery(id+"F6.imprint","IMPRINT",FACE,{"disambiguationData":[TD([[makeQuery(id+"F6.imprint","IMPRINT",EDGE,{"derivedFrom":subQ0}),-1.0]])]});}
            var Q27;
            {var subQ0=sQuery(id+"F6.wireOp",EDGE,"E17.27.0");Q27=makeQuery(id+"F6.imprint","IMPRINT",FACE,{"disambiguationData":[TD([[makeQuery(id+"F6.imprint","IMPRINT",EDGE,{"derivedFrom":subQ0}),-1.0]])]});}
            var Q28;
            {var subQ0=sQuery(id+"F6.wireOp",EDGE,"E17.28.0");Q28=makeQuery(id+"F6.imprint","IMPRINT",FACE,{"disambiguationData":[TD([[makeQuery(id+"F6.imprint","IMPRINT",EDGE,{"derivedFrom":subQ0}),-1.0]])]});}
            var Q29;
            {var subQ0=sQuery(id+"F6.wireOp",EDGE,"E17.29.0");Q29=makeQuery(id+"F6.imprint","IMPRINT",FACE,{"disambiguationData":[TD([[makeQuery(id+"F6.imprint","IMPRINT",EDGE,{"derivedFrom":subQ0}),-1.0]])]});}
            var Q30;
            {var subQ0=sQuery(id+"F6.wireOp",EDGE,"E17.30.0");Q30=makeQuery(id+"F6.imprint","IMPRINT",FACE,{"disambiguationData":[TD([[makeQuery(id+"F6.imprint","IMPRINT",EDGE,{"derivedFrom":subQ0}),-1.0]])]});}
            var Q31;
            {var subQ0=sQuery(id+"F6.wireOp",EDGE,"E17.31.0");Q31=makeQuery(id+"F6.imprint","IMPRINT",FACE,{"disambiguationData":[TD([[makeQuery(id+"F6.imprint","IMPRINT",EDGE,{"derivedFrom":subQ0}),-1.0]])]});}
            var Q32;
            {var subQ0=sQuery(id+"F6.wireOp",EDGE,"E17.32.0");Q32=makeQuery(id+"F6.imprint","IMPRINT",FACE,{"disambiguationData":[TD([[makeQuery(id+"F6.imprint","IMPRINT",EDGE,{"derivedFrom":subQ0}),-1.0]])]});}
            var Q33;
            {var subQ0=sQuery(id+"F6.wireOp",EDGE,"E17.33.0");Q33=makeQuery(id+"F6.imprint","IMPRINT",FACE,{"disambiguationData":[TD([[makeQuery(id+"F6.imprint","IMPRINT",EDGE,{"derivedFrom":subQ0}),-1.0]])]});}
            var Q34;
            {var subQ0=sQuery(id+"F6.wireOp",EDGE,"E17.34.0");Q34=makeQuery(id+"F6.imprint","IMPRINT",FACE,{"disambiguationData":[TD([[makeQuery(id+"F6.imprint","IMPRINT",EDGE,{"derivedFrom":subQ0}),-1.0]])]});}
            var Q35;
            {var subQ0=sQuery(id+"F6.wireOp",EDGE,"E17.35.0");Q35=makeQuery(id+"F6.imprint","IMPRINT",FACE,{"disambiguationData":[TD([[makeQuery(id+"F6.imprint","IMPRINT",EDGE,{"derivedFrom":subQ0}),-1.0]])]});}
            var Q36;
            {var subQ0=sQuery(id+"F6.wireOp",EDGE,"E17.36.0");Q36=makeQuery(id+"F6.imprint","IMPRINT",FACE,{"disambiguationData":[TD([[makeQuery(id+"F6.imprint","IMPRINT",EDGE,{"derivedFrom":subQ0}),-1.0]])]});}
            var Q37;
            {var subQ0=sQuery(id+"F6.wireOp",EDGE,"E17.37.0");Q37=makeQuery(id+"F6.imprint","IMPRINT",FACE,{"disambiguationData":[TD([[makeQuery(id+"F6.imprint","IMPRINT",EDGE,{"derivedFrom":subQ0}),-1.0]])]});}
            var Q38;
            {var subQ0=sQuery(id+"F6.wireOp",EDGE,"E17.38.0");Q38=makeQuery(id+"F6.imprint","IMPRINT",FACE,{"disambiguationData":[TD([[makeQuery(id+"F6.imprint","IMPRINT",EDGE,{"derivedFrom":subQ0}),-1.0]])]});}
            var Q39;
            {var subQ0=sQuery(id+"F6.wireOp",EDGE,"E17.39.0");Q39=makeQuery(id+"F6.imprint","IMPRINT",FACE,{"disambiguationData":[TD([[makeQuery(id+"F6.imprint","IMPRINT",EDGE,{"derivedFrom":subQ0}),-1.0]])]});}
            var Q40;
            {var subQ0=sQuery(id+"F6.wireOp",EDGE,"E17.40.0");Q40=makeQuery(id+"F6.imprint","IMPRINT",FACE,{"disambiguationData":[TD([[makeQuery(id+"F6.imprint","IMPRINT",EDGE,{"derivedFrom":subQ0}),-1.0]])]});}
            var Q41;
            {var subQ0=sQuery(id+"F6.wireOp",EDGE,"E17.41.0");Q41=makeQuery(id+"F6.imprint","IMPRINT",FACE,{"disambiguationData":[TD([[makeQuery(id+"F6.imprint","IMPRINT",EDGE,{"derivedFrom":subQ0}),-1.0]])]});}
            var Q42;
            {var subQ0=sQuery(id+"F6.wireOp",EDGE,"E17.42.0");Q42=makeQuery(id+"F6.imprint","IMPRINT",FACE,{"disambiguationData":[TD([[makeQuery(id+"F6.imprint","IMPRINT",EDGE,{"derivedFrom":subQ0}),-1.0]])]});}
            var Q43;
            {var subQ0=sQuery(id+"F6.wireOp",EDGE,"E17.43.0");Q43=makeQuery(id+"F6.imprint","IMPRINT",FACE,{"disambiguationData":[TD([[makeQuery(id+"F6.imprint","IMPRINT",EDGE,{"derivedFrom":subQ0}),-1.0]])]});}
            var Q44;
            {var subQ0=sQuery(id+"F6.wireOp",EDGE,"E17.44.0");Q44=makeQuery(id+"F6.imprint","IMPRINT",FACE,{"disambiguationData":[TD([[makeQuery(id+"F6.imprint","IMPRINT",EDGE,{"derivedFrom":subQ0}),-1.0]])]});}
            var Q45;
            {var subQ0=sQuery(id+"F6.wireOp",EDGE,"E17.45.0");Q45=makeQuery(id+"F6.imprint","IMPRINT",FACE,{"disambiguationData":[TD([[makeQuery(id+"F6.imprint","IMPRINT",EDGE,{"derivedFrom":subQ0}),-1.0]])]});}
            var Q46;
            {var subQ0=sQuery(id+"F6.wireOp",EDGE,"E17.46.0");Q46=makeQuery(id+"F6.imprint","IMPRINT",FACE,{"disambiguationData":[TD([[makeQuery(id+"F6.imprint","IMPRINT",EDGE,{"derivedFrom":subQ0}),-1.0]])]});}
            var Q47;
            {var subQ0=sQuery(id+"F6.wireOp",EDGE,"E17.47.0");Q47=makeQuery(id+"F6.imprint","IMPRINT",FACE,{"disambiguationData":[TD([[makeQuery(id+"F6.imprint","IMPRINT",EDGE,{"derivedFrom":subQ0}),-1.0]])]});}
            var Q48;
            {var subQ0=sQuery(id+"F6.wireOp",EDGE,"E17.48.0");Q48=makeQuery(id+"F6.imprint","IMPRINT",FACE,{"disambiguationData":[TD([[makeQuery(id+"F6.imprint","IMPRINT",EDGE,{"derivedFrom":subQ0}),-1.0]])]});}
            var Q49;
            {var subQ0=sQuery(id+"F6.wireOp",EDGE,"E17.49.0");Q49=makeQuery(id+"F6.imprint","IMPRINT",FACE,{"disambiguationData":[TD([[makeQuery(id+"F6.imprint","IMPRINT",EDGE,{"derivedFrom":subQ0}),-1.0]])]});}
            var Q50;
            {var subQ0=sQuery(id+"F6.wireOp",EDGE,"E17.50.0");Q50=makeQuery(id+"F6.imprint","IMPRINT",FACE,{"disambiguationData":[TD([[makeQuery(id+"F6.imprint","IMPRINT",EDGE,{"derivedFrom":subQ0}),-1.0]])]});}
            var Q51;
            {var subQ0=sQuery(id+"F6.wireOp",EDGE,"E17.51.0");Q51=makeQuery(id+"F6.imprint","IMPRINT",FACE,{"disambiguationData":[TD([[makeQuery(id+"F6.imprint","IMPRINT",EDGE,{"derivedFrom":subQ0}),-1.0]])]});}
            var Q52;
            {var subQ0=sQuery(id+"F6.wireOp",EDGE,"E17.52.0");Q52=makeQuery(id+"F6.imprint","IMPRINT",FACE,{"disambiguationData":[TD([[makeQuery(id+"F6.imprint","IMPRINT",EDGE,{"derivedFrom":subQ0}),-1.0]])]});}
            var Q53;
            {var subQ0=sQuery(id+"F6.wireOp",EDGE,"E17.53.0");Q53=makeQuery(id+"F6.imprint","IMPRINT",FACE,{"disambiguationData":[TD([[makeQuery(id+"F6.imprint","IMPRINT",EDGE,{"derivedFrom":subQ0}),-1.0]])]});}
            var Q54;
            {var subQ0=sQuery(id+"F6.wireOp",EDGE,"E17.54.0");Q54=makeQuery(id+"F6.imprint","IMPRINT",FACE,{"disambiguationData":[TD([[makeQuery(id+"F6.imprint","IMPRINT",EDGE,{"derivedFrom":subQ0}),-1.0]])]});}
            var Q55;
            {var subQ0=sQuery(id+"F6.wireOp",EDGE,"E17.55.0");Q55=makeQuery(id+"F6.imprint","IMPRINT",FACE,{"disambiguationData":[TD([[makeQuery(id+"F6.imprint","IMPRINT",EDGE,{"derivedFrom":subQ0}),-1.0]])]});}
            var Q56;
            {var subQ0=sQuery(id+"F6.wireOp",EDGE,"E17.56.0");Q56=makeQuery(id+"F6.imprint","IMPRINT",FACE,{"disambiguationData":[TD([[makeQuery(id+"F6.imprint","IMPRINT",EDGE,{"derivedFrom":subQ0}),-1.0]])]});}
            var Q57;
            {var subQ0=sQuery(id+"F6.wireOp",EDGE,"E17.57.0");Q57=makeQuery(id+"F6.imprint","IMPRINT",FACE,{"disambiguationData":[TD([[makeQuery(id+"F6.imprint","IMPRINT",EDGE,{"derivedFrom":subQ0}),-1.0]])]});}
            var Q58;
            {var subQ0=sQuery(id+"F6.wireOp",EDGE,"E17.58.0");Q58=makeQuery(id+"F6.imprint","IMPRINT",FACE,{"disambiguationData":[TD([[makeQuery(id+"F6.imprint","IMPRINT",EDGE,{"derivedFrom":subQ0}),-1.0]])]});}
            var Q59;
            {var subQ0=sQuery(id+"F6.wireOp",EDGE,"E17.59.0");Q59=makeQuery(id+"F6.imprint","IMPRINT",FACE,{"disambiguationData":[TD([[makeQuery(id+"F6.imprint","IMPRINT",EDGE,{"derivedFrom":subQ0}),-1.0]])]});}
            var Q60;
            {var subQ0=sQuery(id+"F6.wireOp",EDGE,"E17.60.0");Q60=makeQuery(id+"F6.imprint","IMPRINT",FACE,{"disambiguationData":[TD([[makeQuery(id+"F6.imprint","IMPRINT",EDGE,{"derivedFrom":subQ0}),-1.0]])]});}
            var Q61;
            {var subQ0=sQuery(id+"F6.wireOp",EDGE,"E17.61.0");Q61=makeQuery(id+"F6.imprint","IMPRINT",FACE,{"disambiguationData":[TD([[makeQuery(id+"F6.imprint","IMPRINT",EDGE,{"derivedFrom":subQ0}),-1.0]])]});}
            var Q62;
            {var subQ0=sQuery(id+"F6.wireOp",EDGE,"E17.62.0");Q62=makeQuery(id+"F6.imprint","IMPRINT",FACE,{"disambiguationData":[TD([[makeQuery(id+"F6.imprint","IMPRINT",EDGE,{"derivedFrom":subQ0}),-1.0]])]});}
            var Q63;
            {var subQ0=sQuery(id+"F6.wireOp",EDGE,"E17.63.0");Q63=makeQuery(id+"F6.imprint","IMPRINT",FACE,{"disambiguationData":[TD([[makeQuery(id+"F6.imprint","IMPRINT",EDGE,{"derivedFrom":subQ0}),-1.0]])]});}
            var Q64;
            {var subQ0=sQuery(id+"F6.wireOp",EDGE,"E17.64.0");Q64=makeQuery(id+"F6.imprint","IMPRINT",FACE,{"disambiguationData":[TD([[makeQuery(id+"F6.imprint","IMPRINT",EDGE,{"derivedFrom":subQ0}),-1.0]])]});}
            var Q65;
            {var subQ0=sQuery(id+"F6.wireOp",EDGE,"E17.65.0");Q65=makeQuery(id+"F6.imprint","IMPRINT",FACE,{"disambiguationData":[TD([[makeQuery(id+"F6.imprint","IMPRINT",EDGE,{"derivedFrom":subQ0}),-1.0]])]});}
            var Q66;
            {var subQ0=sQuery(id+"F6.wireOp",EDGE,"E17.66.0");Q66=makeQuery(id+"F6.imprint","IMPRINT",FACE,{"disambiguationData":[TD([[makeQuery(id+"F6.imprint","IMPRINT",EDGE,{"derivedFrom":subQ0}),-1.0]])]});}
            var Q67;
            {var subQ0=sQuery(id+"F6.wireOp",EDGE,"E17.67.0");Q67=makeQuery(id+"F6.imprint","IMPRINT",FACE,{"disambiguationData":[TD([[makeQuery(id+"F6.imprint","IMPRINT",EDGE,{"derivedFrom":subQ0}),-1.0]])]});}
            var Q68;
            {var subQ0=sQuery(id+"F6.wireOp",EDGE,"E17.68.0");Q68=makeQuery(id+"F6.imprint","IMPRINT",FACE,{"disambiguationData":[TD([[makeQuery(id+"F6.imprint","IMPRINT",EDGE,{"derivedFrom":subQ0}),-1.0]])]});}
            var Q69;
            {var subQ0=sQuery(id+"F6.wireOp",EDGE,"E17.69.0");Q69=makeQuery(id+"F6.imprint","IMPRINT",FACE,{"disambiguationData":[TD([[makeQuery(id+"F6.imprint","IMPRINT",EDGE,{"derivedFrom":subQ0}),-1.0]])]});}
            var Q70;
            {var subQ0=sQuery(id+"F6.wireOp",EDGE,"E17.70.0");Q70=makeQuery(id+"F6.imprint","IMPRINT",FACE,{"disambiguationData":[TD([[makeQuery(id+"F6.imprint","IMPRINT",EDGE,{"derivedFrom":subQ0}),-1.0]])]});}
            var Q71;
            {var subQ0=sQuery(id+"F6.wireOp",EDGE,"E17.71.0");Q71=makeQuery(id+"F6.imprint","IMPRINT",FACE,{"disambiguationData":[TD([[makeQuery(id+"F6.imprint","IMPRINT",EDGE,{"derivedFrom":subQ0}),-1.0]])]});}
            var Q72;
            {var subQ0=sQuery(id+"F6.wireOp",EDGE,"E17.72.0");Q72=makeQuery(id+"F6.imprint","IMPRINT",FACE,{"disambiguationData":[TD([[makeQuery(id+"F6.imprint","IMPRINT",EDGE,{"derivedFrom":subQ0}),-1.0]])]});}
            var Q73;
            {var subQ0=sQuery(id+"F6.wireOp",EDGE,"E17.73.0");Q73=makeQuery(id+"F6.imprint","IMPRINT",FACE,{"disambiguationData":[TD([[makeQuery(id+"F6.imprint","IMPRINT",EDGE,{"derivedFrom":subQ0}),-1.0]])]});}
            var Q74;
            {var subQ0=sQuery(id+"F6.wireOp",EDGE,"E17.74.0");Q74=makeQuery(id+"F6.imprint","IMPRINT",FACE,{"disambiguationData":[TD([[makeQuery(id+"F6.imprint","IMPRINT",EDGE,{"derivedFrom":subQ0}),-1.0]])]});}
            var Q75;
            {var subQ0=sQuery(id+"F6.wireOp",EDGE,"E17.75.0");Q75=makeQuery(id+"F6.imprint","IMPRINT",FACE,{"disambiguationData":[TD([[makeQuery(id+"F6.imprint","IMPRINT",EDGE,{"derivedFrom":subQ0}),-1.0]])]});}
            var Q76;
            {var subQ0=sQuery(id+"F6.wireOp",EDGE,"E17.76.0");Q76=makeQuery(id+"F6.imprint","IMPRINT",FACE,{"disambiguationData":[TD([[makeQuery(id+"F6.imprint","IMPRINT",EDGE,{"derivedFrom":subQ0}),-1.0]])]});}
            var Q77;
            {var subQ0=sQuery(id+"F6.wireOp",EDGE,"E17.77.0");Q77=makeQuery(id+"F6.imprint","IMPRINT",FACE,{"disambiguationData":[TD([[makeQuery(id+"F6.imprint","IMPRINT",EDGE,{"derivedFrom":subQ0}),-1.0]])]});}
            var Q78;
            {var subQ0=sQuery(id+"F6.wireOp",EDGE,"E17.78.0");Q78=makeQuery(id+"F6.imprint","IMPRINT",FACE,{"disambiguationData":[TD([[makeQuery(id+"F6.imprint","IMPRINT",EDGE,{"derivedFrom":subQ0}),-1.0]])]});}
            var Q79;
            {var subQ0=sQuery(id+"F6.wireOp",EDGE,"E17.79.0");Q79=makeQuery(id+"F6.imprint","IMPRINT",FACE,{"disambiguationData":[TD([[makeQuery(id+"F6.imprint","IMPRINT",EDGE,{"derivedFrom":subQ0}),-1.0]])]});}
            var Q80;
            {var subQ0=sQuery(id+"F6.wireOp",EDGE,"E17.80.0");Q80=makeQuery(id+"F6.imprint","IMPRINT",FACE,{"disambiguationData":[TD([[makeQuery(id+"F6.imprint","IMPRINT",EDGE,{"derivedFrom":subQ0}),-1.0]])]});}
            var Q81;
            {var subQ0=sQuery(id+"F6.wireOp",EDGE,"E17.81.0");Q81=makeQuery(id+"F6.imprint","IMPRINT",FACE,{"disambiguationData":[TD([[makeQuery(id+"F6.imprint","IMPRINT",EDGE,{"derivedFrom":subQ0}),-1.0]])]});}
            var Q82;
            {var subQ0=sQuery(id+"F6.wireOp",EDGE,"E17.82.0");Q82=makeQuery(id+"F6.imprint","IMPRINT",FACE,{"disambiguationData":[TD([[makeQuery(id+"F6.imprint","IMPRINT",EDGE,{"derivedFrom":subQ0}),-1.0]])]});}
            var Q83;
            {var subQ0=sQuery(id+"F6.wireOp",EDGE,"E17.83.0");Q83=makeQuery(id+"F6.imprint","IMPRINT",FACE,{"disambiguationData":[TD([[makeQuery(id+"F6.imprint","IMPRINT",EDGE,{"derivedFrom":subQ0}),-1.0]])]});}
            var Q84;
            {var subQ0=sQuery(id+"F6.wireOp",EDGE,"E17.84.0");Q84=makeQuery(id+"F6.imprint","IMPRINT",FACE,{"disambiguationData":[TD([[makeQuery(id+"F6.imprint","IMPRINT",EDGE,{"derivedFrom":subQ0}),-1.0]])]});}
            var Q85;
            {var subQ0=sQuery(id+"F6.wireOp",EDGE,"E17.85.0");Q85=makeQuery(id+"F6.imprint","IMPRINT",FACE,{"disambiguationData":[TD([[makeQuery(id+"F6.imprint","IMPRINT",EDGE,{"derivedFrom":subQ0}),-1.0]])]});}
            var Q86;
            {var subQ0=sQuery(id+"F6.wireOp",EDGE,"E17.86.0");Q86=makeQuery(id+"F6.imprint","IMPRINT",FACE,{"disambiguationData":[TD([[makeQuery(id+"F6.imprint","IMPRINT",EDGE,{"derivedFrom":subQ0}),-1.0]])]});}
            var Q87;
            {var subQ0=sQuery(id+"F6.wireOp",EDGE,"E17.87.0");Q87=makeQuery(id+"F6.imprint","IMPRINT",FACE,{"disambiguationData":[TD([[makeQuery(id+"F6.imprint","IMPRINT",EDGE,{"derivedFrom":subQ0}),-1.0]])]});}
            var Q88;
            {var subQ0=sQuery(id+"F6.wireOp",EDGE,"E17.88.0");Q88=makeQuery(id+"F6.imprint","IMPRINT",FACE,{"disambiguationData":[TD([[makeQuery(id+"F6.imprint","IMPRINT",EDGE,{"derivedFrom":subQ0}),-1.0]])]});}
            var Q89;
            {var subQ0=sQuery(id+"F6.wireOp",EDGE,"E17.89.0");Q89=makeQuery(id+"F6.imprint","IMPRINT",FACE,{"disambiguationData":[TD([[makeQuery(id+"F6.imprint","IMPRINT",EDGE,{"derivedFrom":subQ0}),-1.0]])]});}
            var Q90;
            {var subQ0=sQuery(id+"F6.wireOp",EDGE,"E17.90.0");Q90=makeQuery(id+"F6.imprint","IMPRINT",FACE,{"disambiguationData":[TD([[makeQuery(id+"F6.imprint","IMPRINT",EDGE,{"derivedFrom":subQ0}),-1.0]])]});}
            var Q91;
            {var subQ0=sQuery(id+"F6.wireOp",EDGE,"E17.91.0");Q91=makeQuery(id+"F6.imprint","IMPRINT",FACE,{"disambiguationData":[TD([[makeQuery(id+"F6.imprint","IMPRINT",EDGE,{"derivedFrom":subQ0}),-1.0]])]});}
            var Q92;
            {var subQ0=sQuery(id+"F6.wireOp",EDGE,"E17.92.0");Q92=makeQuery(id+"F6.imprint","IMPRINT",FACE,{"disambiguationData":[TD([[makeQuery(id+"F6.imprint","IMPRINT",EDGE,{"derivedFrom":subQ0}),-1.0]])]});}
            var Q93;
            {var subQ0=sQuery(id+"F6.wireOp",EDGE,"E17.93.0");Q93=makeQuery(id+"F6.imprint","IMPRINT",FACE,{"disambiguationData":[TD([[makeQuery(id+"F6.imprint","IMPRINT",EDGE,{"derivedFrom":subQ0}),-1.0]])]});}
            var Q94;
            {var subQ0=sQuery(id+"F6.wireOp",EDGE,"E17.94.0");Q94=makeQuery(id+"F6.imprint","IMPRINT",FACE,{"disambiguationData":[TD([[makeQuery(id+"F6.imprint","IMPRINT",EDGE,{"derivedFrom":subQ0}),-1.0]])]});}
            var Q95;
            {var subQ0=sQuery(id+"F6.wireOp",EDGE,"E17.95.0");Q95=makeQuery(id+"F6.imprint","IMPRINT",FACE,{"disambiguationData":[TD([[makeQuery(id+"F6.imprint","IMPRINT",EDGE,{"derivedFrom":subQ0}),-1.0]])]});}
            var Q96;
            {var subQ0=sQuery(id+"F6.wireOp",EDGE,"E17.96.0");Q96=makeQuery(id+"F6.imprint","IMPRINT",FACE,{"disambiguationData":[TD([[makeQuery(id+"F6.imprint","IMPRINT",EDGE,{"derivedFrom":subQ0}),-1.0]])]});}
            var Q97;
            {var subQ0=sQuery(id+"F6.wireOp",EDGE,"E17.97.0");Q97=makeQuery(id+"F6.imprint","IMPRINT",FACE,{"disambiguationData":[TD([[makeQuery(id+"F6.imprint","IMPRINT",EDGE,{"derivedFrom":subQ0}),-1.0]])]});}
            var Q98;
            {var subQ0=sQuery(id+"F6.wireOp",EDGE,"E17.98.0");Q98=makeQuery(id+"F6.imprint","IMPRINT",FACE,{"disambiguationData":[TD([[makeQuery(id+"F6.imprint","IMPRINT",EDGE,{"derivedFrom":subQ0}),-1.0]])]});}
            var Q99;
            {var subQ0=sQuery(id+"F6.wireOp",EDGE,"E17.99.0");Q99=makeQuery(id+"F6.imprint","IMPRINT",FACE,{"disambiguationData":[TD([[makeQuery(id+"F6.imprint","IMPRINT",EDGE,{"derivedFrom":subQ0}),-1.0]])]});}
            var Q100;
            Q100=makeQuery(id+"F6.imprint","IMPRINT",FACE,{"disambiguationData":[TD([[makeQuery(id+"F6.imprint","IMPRINT",EDGE,{"derivedFrom":makeQuery(id+"F5.opExtrude","CAP_EDGE",EDGE,{"disambiguationData":[OSD([sQuery(id+"F4.wireOp",EDGE,"E12")])],"isStart":false})}),-1.0]])]});
            extrude(context, id + "F7", {"entities" : qUnion([Q0, Q1, Q2, Q3, Q4, Q5, Q6, Q7, Q8, Q9, Q10, Q11, Q12, Q13, Q14, Q15, Q16, Q17, Q18, Q19, Q20, Q21, Q22, Q23, Q24, Q25, Q26, Q27, Q28, Q29, Q30, Q31, Q32, Q33, Q34, Q35, Q36, Q37, Q38, Q39, Q40, Q41, Q42, Q43, Q44, Q45, Q46, Q47, Q48, Q49, Q50, Q51, Q52, Q53, Q54, Q55, Q56, Q57, Q58, Q59, Q60, Q61, Q62, Q63, Q64, Q65, Q66, Q67, Q68, Q69, Q70, Q71, Q72, Q73, Q74, Q75, Q76, Q77, Q78, Q79, Q80, Q81, Q82, Q83, Q84, Q85, Q86, Q87, Q88, Q89, Q90, Q91, Q92, Q93, Q94, Q95, Q96, Q97, Q98, Q99, Q100]), "operationType" : NewBodyOperationType.ADD, "oppositeDirection" : true, "depth" : 5.08 * mm});
        }
    });
